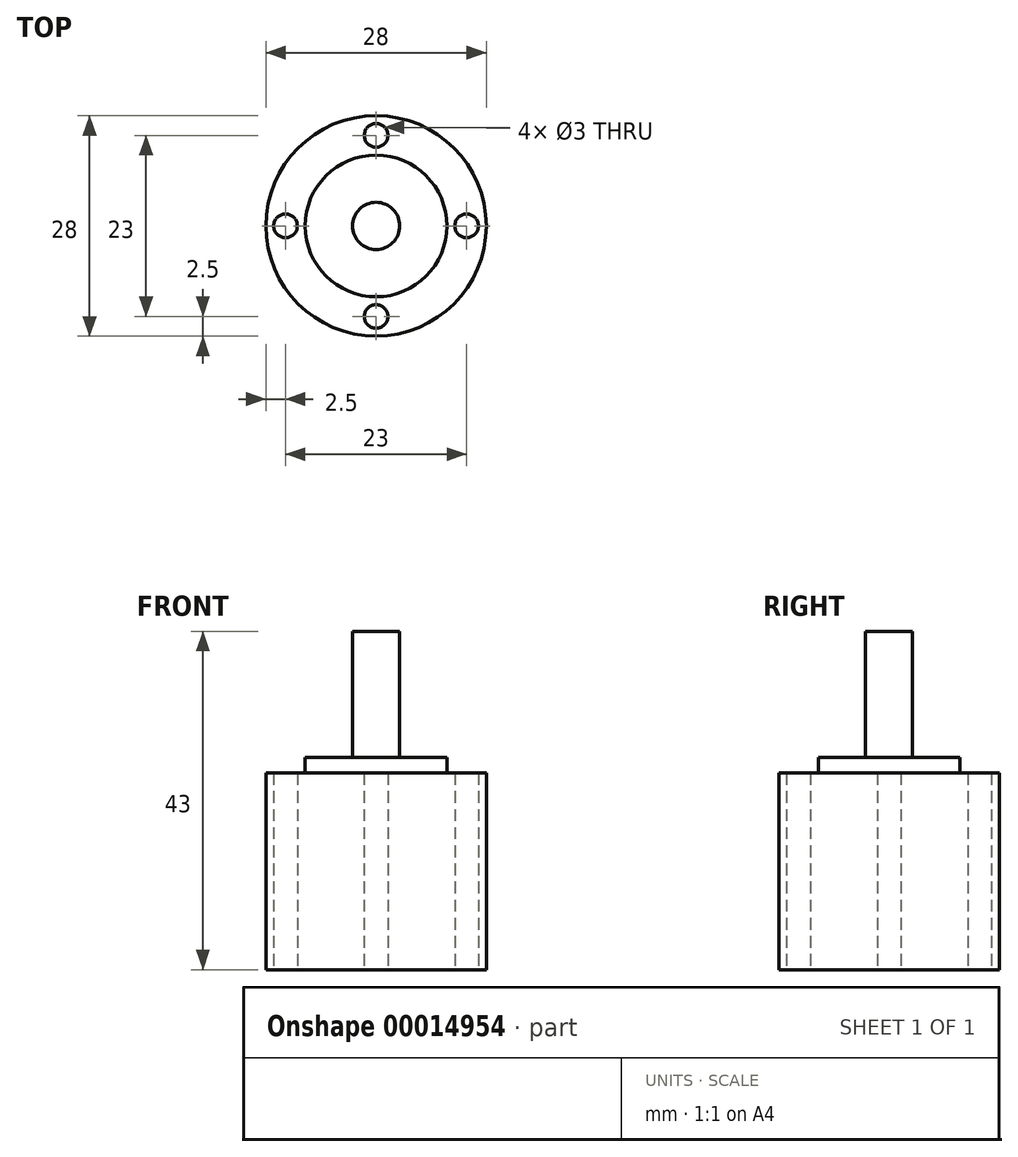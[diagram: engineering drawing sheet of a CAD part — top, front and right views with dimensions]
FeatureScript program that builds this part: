
annotation { "Feature Type Name" : "Feature", "Feature Type Description" : "" }
export const myFeature = defineFeature(function(context is Context, id is Id, definition is map)
    precondition{}
    {
        {
            var Q0;
            Q0=qCreatedBy(makeId("Top.planeOp"),FACE);
            var sketch = newSketch(context, id + "F0", { "sketchPlane" : qUnion([Q0])});
            skCircle(sketch, "E0", {"center": v(0, 0) * mm, "radius": 14 * mm});
            skCircle(sketch, "E1", {"center": v(-11.5, 0) * mm, "radius": 1.5 * mm});
            skCircle(sketch, "E2.1.0", {"center": v(0, -11.5) * mm, "radius": 1.5 * mm});
            skCircle(sketch, "E2.2.0", {"center": v(11.5, 0) * mm, "radius": 1.5 * mm});
            skCircle(sketch, "E2.3.0", {"center": v(0, 11.5) * mm, "radius": 1.5 * mm});
            skSolve(sketch);
        }
        {
            var Q0;
            Q0=makeQuery(id+"F0.imprint","IMPRINT",FACE,{"disambiguationData":[TD([[makeQuery(id+"F0.imprint","IMPRINT",EDGE,{"derivedFrom":sQuery(id+"F0.wireOp",EDGE,"E0")}),1.0]])]});
            extrude(context, id + "F1", {"entities" : qUnion([Q0]), "depth" : 25 * mm});
        }
        {
            var Q0;
            Q0=makeQuery(id+"F1.opExtrude","CAP_FACE",FACE,{"disambiguationData":[OSD([sQuery(id+"F0.wireOp",EDGE,"E0"),sQuery(id+"F0.wireOp",EDGE,"E1"),sQuery(id+"F0.wireOp",EDGE,"E2.1.0"),sQuery(id+"F0.wireOp",EDGE,"E2.2.0"),sQuery(id+"F0.wireOp",EDGE,"E2.3.0")])],"isStart":false});
            var sketch = newSketch(context, id + "F2", { "sketchPlane" : qUnion([Q0])});
            skCircle(sketch, "E3", {"center": v(0, 0) * mm, "radius": 9 * mm});
            skSolve(sketch);
        }
        {
            var Q0;
            Q0=qSketchRegion(id+"F2",true);
            extrude(context, id + "F3", {"entities" : qUnion([Q0]), "operationType" : NewBodyOperationType.ADD, "depth" : 2 * mm});
        }
        {
            var Q0;
            Q0=makeQuery(id+"F3.opExtrude","CAP_FACE",FACE,{"disambiguationData":[OSD([sQuery(id+"F2.wireOp",EDGE,"E3")])],"isStart":false});
            var sketch = newSketch(context, id + "F4", { "sketchPlane" : qUnion([Q0])});
            skCircle(sketch, "E4", {"center": v(0, 0) * mm, "radius": 3 * mm});
            skSolve(sketch);
        }
        {
            var Q0;
            Q0=qSketchRegion(id+"F4",true);
            extrude(context, id + "F5", {"entities" : qUnion([Q0]), "operationType" : NewBodyOperationType.ADD, "depth" : 16 * mm});
        }
    });
